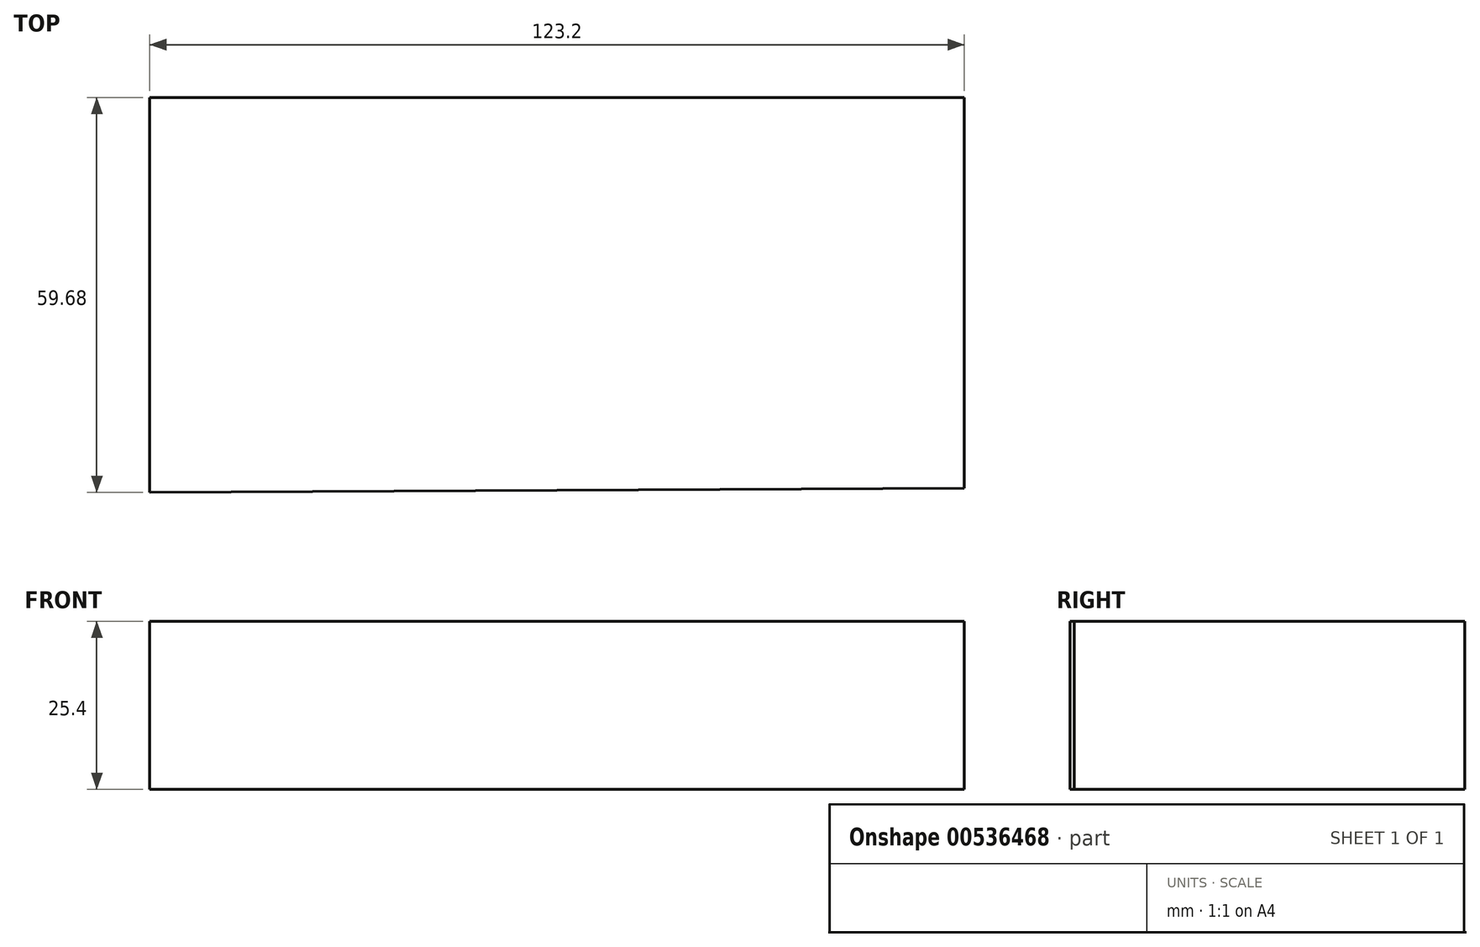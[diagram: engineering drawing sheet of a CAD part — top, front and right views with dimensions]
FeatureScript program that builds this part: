
annotation { "Feature Type Name" : "Feature", "Feature Type Description" : "" }
export const myFeature = defineFeature(function(context is Context, id is Id, definition is map)
    precondition{}
    {
        {
            var Q0;
            Q0=qCreatedBy(makeId("Top.planeOp"),FACE);
            var sketch = newSketch(context, id + "F0", { "sketchPlane" : qUnion([Q0])});
            skLineSegment(sketch, "E0.bottom", {"start": v(-63.42, 31.9) * mm, "end": v(63.42, 31.9) * mm});
            skLineSegment(sketch, "E0.top", {"start": v(-63.42, -31.9) * mm, "end": v(63.42, -31.9) * mm});
            skLineSegment(sketch, "E0.left", {"start": v(-63.42, 31.9) * mm, "end": v(-63.42, -31.9) * mm});
            skLineSegment(sketch, "E0.right", {"start": v(63.42, 31.9) * mm, "end": v(63.42, -31.9) * mm});
            skPoint(sketch, "E0.middle", {"position": v(0, 0) * mm});
            skSolve(sketch);
        }
        {
            var Q0;
            Q0=makeQuery(id+"F0.imprint","IMPRINT",FACE,{"disambiguationData":[TD([[makeQuery(id+"F0.imprint","IMPRINT",EDGE,{"derivedFrom":sQuery(id+"F0.wireOp",EDGE,"E0.bottom")}),-1.0]])]});
            var sketch = newSketch(context, id + "F1", { "sketchPlane" : qUnion([Q0])});
            skLineSegment(sketch, "E1", {"start": v(-62.33, 32.08) * mm, "end": v(-62.33, -31.35) * mm});
            skLineSegment(sketch, "E2", {"start": v(-62.33, 30.07) * mm, "end": v(60.87, 30.07) * mm});
            skLineSegment(sketch, "E3", {"start": v(60.87, 30.07) * mm, "end": v(60.87, -31.35) * mm});
            skLineSegment(sketch, "E4", {"start": v(60.87, -31.35) * mm, "end": v(60.87, -28.98) * mm});
            skLineSegment(sketch, "E5", {"start": v(60.87, -28.98) * mm, "end": v(63.6, -28.98) * mm});
            skLineSegment(sketch, "E6", {"start": v(63.6, 30.07) * mm, "end": v(60.87, 30.07) * mm});
            skLineSegment(sketch, "E7", {"start": v(-62.33, 30.07) * mm, "end": v(-63.44, 30.07) * mm});
            skLineSegment(sketch, "E8", {"start": v(-62.33, -31.35) * mm, "end": v(-62.33, -31.94) * mm});
            skLineSegment(sketch, "E9", {"start": v(-62.33, -29.6) * mm, "end": v(-63.44, -29.6) * mm});
            skLineSegment(sketch, "E10", {"start": v(-62.33, -29.6) * mm, "end": v(60.87, -28.98) * mm});
            skSolve(sketch);
        }
        {
            var Q0;
            Q0 = qSketchRegion(id + "F1", true);
            extrude(context, id + "F2", {"entities" : qUnion([Q0]), "depth" : 25.4 * mm, "offsetDistance" : 25.4 * mm});
        }
    });
